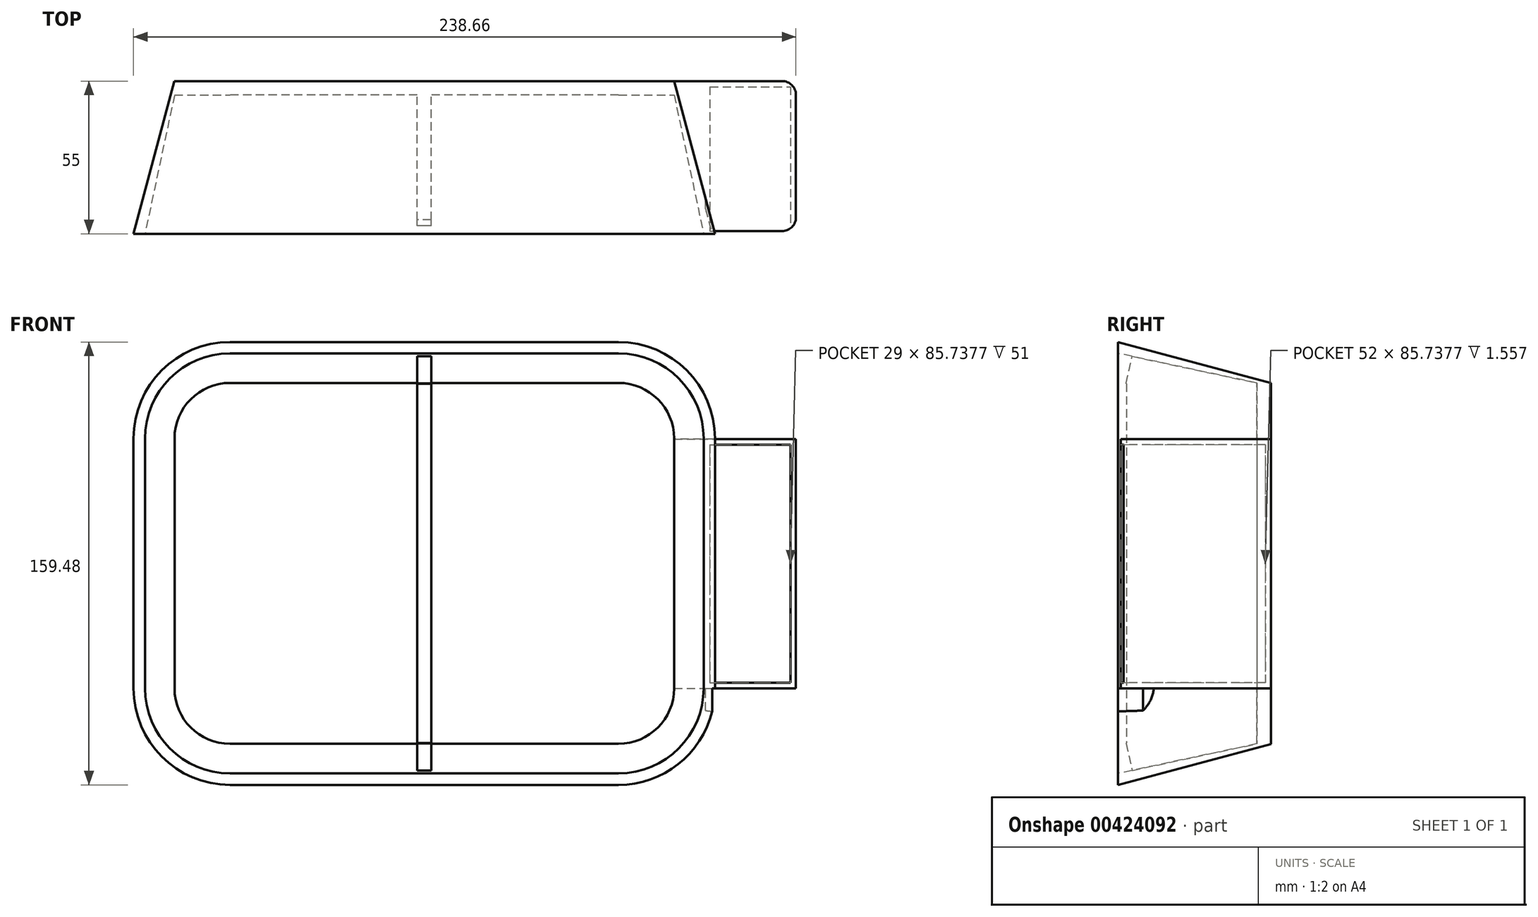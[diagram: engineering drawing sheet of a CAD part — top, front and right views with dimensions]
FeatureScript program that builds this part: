
annotation { "Feature Type Name" : "Feature", "Feature Type Description" : "" }
export const myFeature = defineFeature(function(context is Context, id is Id, definition is map)
    precondition{}
    {
        {
            var Q0;
            Q0=qCreatedBy(makeId("Front.planeOp"),FACE);
            var sketch = newSketch(context, id + "F0", { "sketchPlane" : qUnion([Q0])});
            skLineSegment(sketch, "E0.bottom", {"start": v(-105.92, 85.19) * mm, "end": v(34.08, 85.19) * mm});
            skLineSegment(sketch, "E0.top", {"start": v(-105.92, -44.81) * mm, "end": v(34.08, -44.81) * mm});
            skLineSegment(sketch, "E0.left", {"start": v(-125.92, 65.19) * mm, "end": v(-125.92, -24.81) * mm});
            skLineSegment(sketch, "E0.right", {"start": v(54.08, 65.19) * mm, "end": v(54.08, -24.81) * mm});
            skPoint(sketch, "E1.visualSharp", {"position": v(54.08, 85.19) * mm});
            skArc(sketch, "E1.filletArc", {"start": v(54.08, 65.19) * mm, "mid": v(48.22, 79.33) * mm, "end": v(34.08, 85.19) * mm});
            skArc(sketch, "E2.filletArc", {"start": v(34.08, -44.81) * mm, "mid": v(48.22, -38.95) * mm, "end": v(54.08, -24.81) * mm});
            skArc(sketch, "E3.filletArc", {"start": v(-125.92, -24.81) * mm, "mid": v(-120.06, -38.95) * mm, "end": v(-105.92, -44.81) * mm});
            skPoint(sketch, "E4.visualSharp", {"position": v(-125.92, 85.19) * mm});
            skArc(sketch, "E4.filletArc", {"start": v(-105.92, 85.19) * mm, "mid": v(-120.06, 79.33) * mm, "end": v(-125.92, 65.19) * mm});
            skSolve(sketch);
        }
        {
            var Q0;
            Q0=makeQuery(id+"F0.imprint","IMPRINT",FACE,{"disambiguationData":[TD([[makeQuery(id+"F0.imprint","IMPRINT",EDGE,{"derivedFrom":sQuery(id+"F0.wireOp",EDGE,"E0.bottom")}),-1.0]])]});
            extrude(context, id + "F1", {"entities" : qUnion([Q0]), "depth" : 55 * mm, "hasDraft" : true, "draftAngle" : 15 * degree});
        }
        {
            var Q0;
            Q0=makeQuery(id+"F1.opExtrude","CAP_FACE",FACE,{"disambiguationData":[OSD([sQuery(id+"F0.wireOp",EDGE,"E0.bottom"),sQuery(id+"F0.wireOp",EDGE,"E0.top"),sQuery(id+"F0.wireOp",EDGE,"E0.left"),sQuery(id+"F0.wireOp",EDGE,"E0.right"),sQuery(id+"F0.wireOp",EDGE,"E1.filletArc"),sQuery(id+"F0.wireOp",EDGE,"E2.filletArc"),sQuery(id+"F0.wireOp",EDGE,"E3.filletArc"),sQuery(id+"F0.wireOp",EDGE,"E4.filletArc")])],"isStart":false});
            cPlane(context, id + "F2", {"entities" : qUnion([Q0]), "cplaneType" : CPlaneType.OFFSET, "offset" : 50 * mm, "oppositeDirection" : true, "width" : 150 * mm, "height" : 150 * mm});
        }
        {
            var Q0;
            Q0=qCreatedBy(id+"F2.planeOp",FACE);
            var sketch = newSketch(context, id + "F3", { "sketchPlane" : qUnion([Q0])});
            skLineSegment(sketch, "E5.bottom", {"start": v(-105.9, 85.22) * mm, "end": v(34.1, 85.22) * mm});
            skLineSegment(sketch, "E5.top", {"start": v(-105.9, -44.78) * mm, "end": v(34.1, -44.78) * mm});
            skLineSegment(sketch, "E5.left", {"start": v(-125.9, 65.22) * mm, "end": v(-125.9, -24.78) * mm});
            skLineSegment(sketch, "E5.right", {"start": v(54.1, 65.22) * mm, "end": v(54.1, -24.78) * mm});
            skPoint(sketch, "E6.visualSharp", {"position": v(-125.9, 85.22) * mm});
            skArc(sketch, "E6.filletArc", {"start": v(-105.9, 85.22) * mm, "mid": v(-120.04, 79.36) * mm, "end": v(-125.9, 65.22) * mm});
            skPoint(sketch, "E7.visualSharp", {"position": v(-125.9, -44.78) * mm});
            skArc(sketch, "E7.filletArc", {"start": v(-125.9, -24.78) * mm, "mid": v(-120.04, -38.92) * mm, "end": v(-105.9, -44.78) * mm});
            skPoint(sketch, "E8.visualSharp", {"position": v(54.1, -44.78) * mm});
            skArc(sketch, "E8.filletArc", {"start": v(34.1, -44.78) * mm, "mid": v(48.25, -38.92) * mm, "end": v(54.1, -24.78) * mm});
            skPoint(sketch, "E9.visualSharp", {"position": v(54.1, 85.22) * mm});
            skArc(sketch, "E9.filletArc", {"start": v(54.1, 65.22) * mm, "mid": v(48.25, 79.36) * mm, "end": v(34.1, 85.22) * mm});
            skSolve(sketch);
        }
        {
            var Q0;
            Q0=qSketchRegion(id+"F3",true);
            extrude(context, id + "F4", {"entities" : qUnion([Q0]), "operationType" : NewBodyOperationType.REMOVE, "depth" : 55 * mm, "hasDraft" : true, "draftAngle" : 12 * degree});
        }
        {
            var Q0;
            Q0=makeQuery(id+"F4.boolean.opBoolean","COPY",FACE,{"derivedFrom":makeQuery(id+"F4.opExtrude","CAP_FACE",FACE,{"disambiguationData":[OSD([sQuery(id+"F3.wireOp",EDGE,"E5.bottom"),sQuery(id+"F3.wireOp",EDGE,"E5.top"),sQuery(id+"F3.wireOp",EDGE,"E5.left"),sQuery(id+"F3.wireOp",EDGE,"E5.right"),sQuery(id+"F3.wireOp",EDGE,"E6.filletArc"),sQuery(id+"F3.wireOp",EDGE,"E7.filletArc"),sQuery(id+"F3.wireOp",EDGE,"E8.filletArc"),sQuery(id+"F3.wireOp",EDGE,"E9.filletArc")])],"isStart":true})});
            var sketch = newSketch(context, id + "F5", { "sketchPlane" : qUnion([Q0])});
            skLineSegment(sketch, "E10.bottom", {"start": v(-38.4, 85.22) * mm, "end": v(-33.4, 85.22) * mm});
            skLineSegment(sketch, "E10.top", {"start": v(-38.4, -64.78) * mm, "end": v(-33.4, -64.78) * mm});
            skLineSegment(sketch, "E10.left", {"start": v(-38.4, 85.22) * mm, "end": v(-38.4, -64.78) * mm});
            skLineSegment(sketch, "E10.right", {"start": v(-33.4, 85.22) * mm, "end": v(-33.4, -64.78) * mm});
            skSolve(sketch);
        }
        {
            var Q0;
            Q0=makeQuery(id+"F5.imprint","IMPRINT",FACE,{"disambiguationData":[TD([[makeQuery(id+"F5.imprint","IMPRINT",EDGE,{"derivedFrom":sQuery(id+"F5.wireOp",EDGE,"E10.bottom")}),-1.0]])]});
            extrude(context, id + "F6", {"entities" : qUnion([Q0]), "operationType" : NewBodyOperationType.ADD, "depth" : 47 * mm});
        }
        {
            var Q0;
            Q0=qCreatedBy(makeId("Right.planeOp"),FACE);
            cPlane(context, id + "F7", {"entities" : qUnion([Q0]), "cplaneType" : CPlaneType.OFFSET, "offset" : 98 * mm, "width" : 150 * mm, "height" : 150 * mm});
        }
        {
            var Q0;
            Q0=qCreatedBy(id+"F7.planeOp",FACE);
            var sketch = newSketch(context, id + "F8", { "sketchPlane" : qUnion([Q0])});
            skLineSegment(sketch, "E11.bottom", {"start": v(-54.03, 64.93) * mm, "end": v(0, 64.93) * mm});
            skLineSegment(sketch, "E11.top", {"start": v(-54.03, -25.17) * mm, "end": v(0, -25.17) * mm});
            skLineSegment(sketch, "E11.left", {"start": v(-54.03, 64.93) * mm, "end": v(-54.03, -25.17) * mm});
            skLineSegment(sketch, "E11.right", {"start": v(0, 64.93) * mm, "end": v(0, -25.17) * mm});
            skSolve(sketch);
        }
        {
            var Q0;
            Q0=makeQuery(id+"F1.opExtrude","SWEPT_FACE",FACE,{"disambiguationData":[OSD([sQuery(id+"F0.wireOp",EDGE,"E0.right")])]});
            var sketch = newSketch(context, id + "F9", { "sketchPlane" : qUnion([Q0])});
            skLineSegment(sketch, "E12.bottom", {"start": v(-69.94, 64.93) * mm, "end": v(-14, 64.93) * mm});
            skLineSegment(sketch, "E12.top", {"start": v(-69.94, -24.81) * mm, "end": v(-14, -24.81) * mm});
            skLineSegment(sketch, "E12.left", {"start": v(-69.94, 64.93) * mm, "end": v(-69.94, -24.81) * mm});
            skLineSegment(sketch, "E12.right", {"start": v(-14, 64.93) * mm, "end": v(-14, -24.81) * mm});
            skSolve(sketch);
        }
        {
            var Q0;
            Q0=qCreatedBy(makeId("Front.planeOp"),FACE);
            var sketch = newSketch(context, id + "F10", { "sketchPlane" : qUnion([Q0])});
            skLineSegment(sketch, "E13.bottom", {"start": v(185.4, 123.91) * mm, "end": v(-174.62, 123.91) * mm});
            skLineSegment(sketch, "E13.top", {"start": v(185.4, -101.96) * mm, "end": v(-174.62, -101.96) * mm});
            skLineSegment(sketch, "E13.left", {"start": v(185.4, 123.91) * mm, "end": v(185.4, -101.96) * mm});
            skLineSegment(sketch, "E13.right", {"start": v(-174.62, 123.91) * mm, "end": v(-174.62, -101.96) * mm});
            skSolve(sketch);
        }
        {
            var Q0;
            Q0=qSketchRegion(id+"F10",true);
            extrude(context, id + "F11", {"entities" : qUnion([Q0]), "operationType" : NewBodyOperationType.REMOVE, "oppositeDirection" : true, "depth" : 25 * mm});
        }
        {
            var Q0;
            Q0=makeQuery(id+"F4.boolean.opBoolean","COPY",FACE,{"derivedFrom":makeQuery(id+"F4.opExtrude","SWEPT_FACE",FACE,{"disambiguationData":[OSD([sQuery(id+"F3.wireOp",EDGE,"E5.top")])]})});
            var sketch = newSketch(context, id + "F12", { "sketchPlane" : qUnion([Q0])});
            skLineSegment(sketch, "E14.bottom", {"start": v(-33.4, -60.2) * mm, "end": v(-38.4, -60.2) * mm});
            skLineSegment(sketch, "E14.top", {"start": v(-33.4, -14.2) * mm, "end": v(-38.4, -14.2) * mm});
            skLineSegment(sketch, "E14.left", {"start": v(-33.4, -60.2) * mm, "end": v(-33.4, -14.2) * mm});
            skLineSegment(sketch, "E14.right", {"start": v(-38.4, -60.2) * mm, "end": v(-38.4, -14.2) * mm});
            skSolve(sketch);
        }
        {
            var Q0;
            Q0=qSketchRegion(id+"F12",true);
            extrude(context, id + "F13", {"entities" : qUnion([Q0]), "operationType" : NewBodyOperationType.ADD, "depth" : 10 * mm});
        }
        {
            var Q0;
            Q0=makeQuery(id+"F4.boolean.opBoolean","COPY",FACE,{"derivedFrom":makeQuery(id+"F4.opExtrude","SWEPT_FACE",FACE,{"disambiguationData":[OSD([sQuery(id+"F3.wireOp",EDGE,"E5.bottom")])]})});
            var sketch = newSketch(context, id + "F14", { "sketchPlane" : qUnion([Q0])});
            skLineSegment(sketch, "E15.bottom", {"start": v(-38.4, 68.6) * mm, "end": v(-33.4, 68.6) * mm});
            skLineSegment(sketch, "E15.top", {"start": v(-38.4, 22.6) * mm, "end": v(-33.4, 22.6) * mm});
            skLineSegment(sketch, "E15.left", {"start": v(-38.4, 68.6) * mm, "end": v(-38.4, 22.6) * mm});
            skLineSegment(sketch, "E15.right", {"start": v(-33.4, 68.6) * mm, "end": v(-33.4, 22.6) * mm});
            skSolve(sketch);
        }
        {
            var Q0;
            Q0=makeQuery(id+"F14.imprint","IMPRINT",FACE,{"disambiguationData":[TD([[makeQuery(id+"F14.imprint","IMPRINT",EDGE,{"derivedFrom":sQuery(id+"F14.wireOp",EDGE,"E15.bottom")}),-1.0]])]});
            extrude(context, id + "F15", {"entities" : qUnion([Q0]), "operationType" : NewBodyOperationType.ADD, "depth" : 10 * mm});
        }
        {
            var Q0;
            Q0=makeQuery(id+"F8.imprint","IMPRINT",FACE,{"disambiguationData":[TD([[makeQuery(id+"F8.imprint","IMPRINT",EDGE,{"derivedFrom":sQuery(id+"F8.wireOp",EDGE,"E11.bottom")}),-1.0]])]});
            extrude(context, id + "F16", {"entities" : qUnion([Q0]), "operationType" : NewBodyOperationType.ADD, "oppositeDirection" : true, "depth" : 32.6 * mm});
        }
        {
            var Q0;
            Q0=makeQuery(id+"F9.imprint","IMPRINT",FACE,{"disambiguationData":[TD([[makeQuery(id+"F9.imprint","IMPRINT",EDGE,{"derivedFrom":sQuery(id+"F9.wireOp",EDGE,"E12.bottom")}),-1.0]])]});
            extrude(context, id + "F17", {"entities" : qUnion([Q0]), "operationType" : NewBodyOperationType.ADD, "depth" : 25 * mm});
        }
        {
            var Q0;
            Q0=qCreatedBy(makeId("Front.planeOp"),FACE);
            var sketch = newSketch(context, id + "F18", { "sketchPlane" : qUnion([Q0])});
            skLineSegment(sketch, "E16.bottom", {"start": v(-173.75, 128.8) * mm, "end": v(173.98, 128.8) * mm});
            skLineSegment(sketch, "E16.top", {"start": v(-173.75, -88.43) * mm, "end": v(173.98, -88.43) * mm});
            skLineSegment(sketch, "E16.left", {"start": v(-173.75, 128.8) * mm, "end": v(-173.75, -88.43) * mm});
            skLineSegment(sketch, "E16.right", {"start": v(173.98, 128.8) * mm, "end": v(173.98, -88.43) * mm});
            skSolve(sketch);
        }
        {
            var Q0;
            Q0=qSketchRegion(id+"F18",true);
            extrude(context, id + "F19", {"entities" : qUnion([Q0]), "operationType" : NewBodyOperationType.REMOVE, "oppositeDirection" : true, "depth" : 25 * mm});
        }
        {
            var Q0;
            Q0=makeQuery(id+"F17.opExtrude","SWEPT_FACE",FACE,{"disambiguationData":[OSD([sQuery(id+"F9.wireOp",EDGE,"E12.top")])]});
            var sketch = newSketch(context, id + "F20", { "sketchPlane" : qUnion([Q0])});
            skLineSegment(sketch, "E17.bottom", {"start": v(65.4, 45.99) * mm, "end": v(99.8, 45.99) * mm});
            skLineSegment(sketch, "E17.top", {"start": v(65.4, 0) * mm, "end": v(99.8, 0) * mm});
            skLineSegment(sketch, "E17.left", {"start": v(65.4, 45.99) * mm, "end": v(65.4, 0) * mm});
            skLineSegment(sketch, "E17.right", {"start": v(99.8, 45.99) * mm, "end": v(99.8, 0) * mm});
            skPoint(sketch, "E18.end.orphan", {"position": v(97.92, 45.99) * mm});
            skLineSegment(sketch, "E19", {"start": v(65.4, 45.99) * mm, "end": v(68.02, 55.75) * mm});
            skLineSegment(sketch, "E20", {"start": v(68.02, 55.75) * mm, "end": v(100.28, 55.75) * mm});
            skLineSegment(sketch, "E21", {"start": v(100.28, 55.75) * mm, "end": v(99.8, 45.99) * mm});
            skSolve(sketch);
        }
        {
            var Q0;
            Q0=qSketchRegion(id+"F20",true);
            extrude(context, id + "F21", {"entities" : qUnion([Q0]), "operationType" : NewBodyOperationType.REMOVE, "depth" : 25 * mm});
        }
        {
            var Q0;
            {var subQ0=sQuery(id+"F8.wireOp",EDGE,"E11.left");var subQ1=sQuery(id+"F8.wireOp",EDGE,"E11.bottom");var subQ3=makeQuery(id+"F16.opExtrude","SWEPT_FACE",FACE,{"disambiguationData":[OSD([subQ0])]});Q0=makeQuery(id+"F21.boolean.opBoolean","SPLIT",FACE,{"disambiguationData":[TD([makeQuery(id+"F16.opExtrude","SWEPT_FACE",FACE,{"disambiguationData":[OSD([subQ1])]})])],"derivedFrom":subQ3});}
            var sketch = newSketch(context, id + "F22", { "sketchPlane" : qUnion([Q0])});
            skLineSegment(sketch, "E22.bottom", {"start": v(67, 62.93) * mm, "end": v(96, 62.93) * mm});
            skLineSegment(sketch, "E22.top", {"start": v(67, -22.81) * mm, "end": v(96, -22.81) * mm});
            skLineSegment(sketch, "E22.left", {"start": v(67, 62.93) * mm, "end": v(67, -22.81) * mm});
            skLineSegment(sketch, "E22.right", {"start": v(96, 62.93) * mm, "end": v(96, -22.81) * mm});
            skSolve(sketch);
        }
        {
            var Q0;
            Q0=makeQuery(id+"F22.imprint","IMPRINT",FACE,{"disambiguationData":[TD([[makeQuery(id+"F22.imprint","IMPRINT",EDGE,{"derivedFrom":sQuery(id+"F22.wireOp",EDGE,"E22.bottom")}),-1.0]])]});
            extrude(context, id + "F23", {"entities" : qUnion([Q0]), "operationType" : NewBodyOperationType.REMOVE, "oppositeDirection" : true, "depth" : 52 * mm});
        }
        {
            var Q0;
            Q0=makeQuery(id+"F16.opExtrude","CAP_EDGE",EDGE,{"disambiguationData":[OSD([sQuery(id+"F8.wireOp",EDGE,"E11.left")])],"isStart":true});
            var Q1;
            Q1=makeQuery(id+"F16.opExtrude","CAP_EDGE",EDGE,{"disambiguationData":[OSD([sQuery(id+"F8.wireOp",EDGE,"E11.right")])],"isStart":true});
            fillet(context, id + "F24", {"entities" : qUnion([Q0, Q1]), "radius" : 5 * mm, "tangentPropagation" : true, "allowEdgeOverflow" : false});
        }
    });
